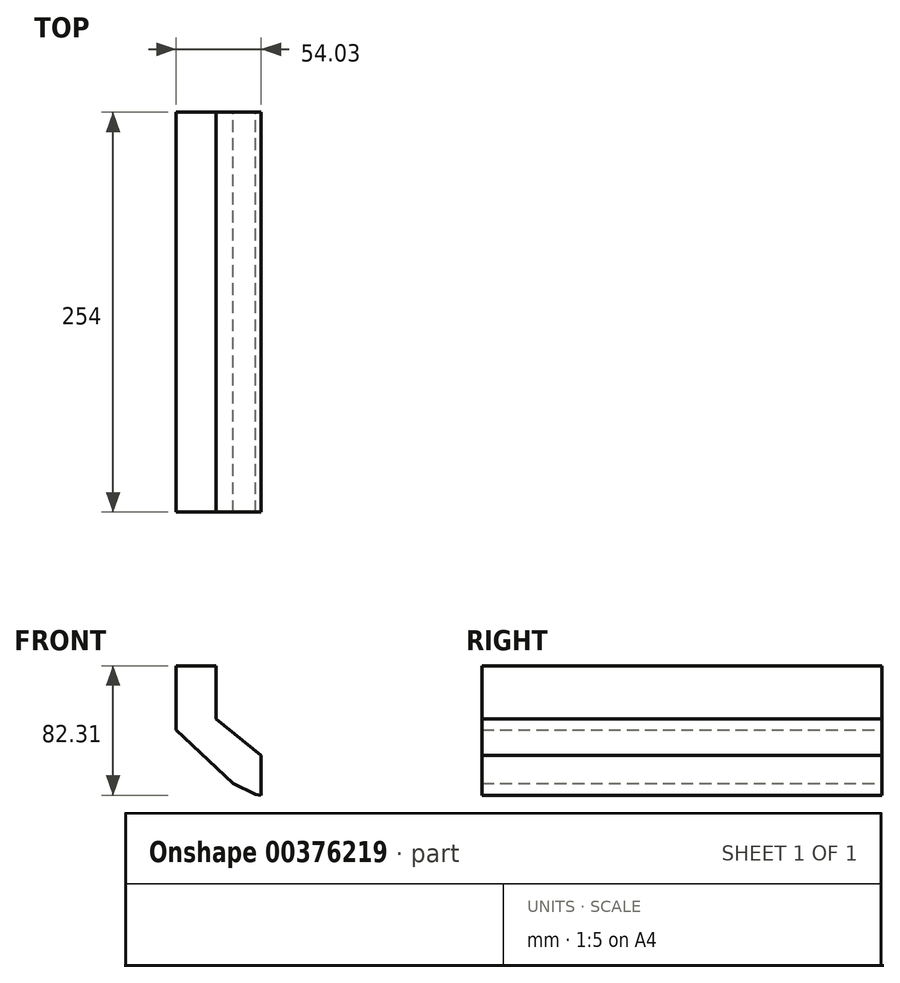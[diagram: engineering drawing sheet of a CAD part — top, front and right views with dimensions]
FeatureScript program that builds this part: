
annotation { "Feature Type Name" : "Feature", "Feature Type Description" : "" }
export const myFeature = defineFeature(function(context is Context, id is Id, definition is map)
    precondition{}
    {
        {
            var Q0;
            Q0=qCreatedBy(makeId("Front.planeOp"),FACE);
            var sketch = newSketch(context, id + "F0", { "sketchPlane" : qUnion([Q0])});
            skLineSegment(sketch, "E0", {"start": v(-75.11, 59.67) * mm, "end": v(-75.11, 18.74) * mm});
            skLineSegment(sketch, "E1", {"start": v(-75.11, 18.74) * mm, "end": v(-39.14, -14.99) * mm});
            skLineSegment(sketch, "E2", {"start": v(-39.14, -14.99) * mm, "end": v(-24.7, -22.2) * mm});
            skLineSegment(sketch, "E3", {"start": v(-75.11, 59.67) * mm, "end": v(-49.71, 59.67) * mm});
            skLineSegment(sketch, "E4", {"start": v(-21.08, 2.69) * mm, "end": v(-21.08, -22.64) * mm});
            skLineSegment(sketch, "E5", {"start": v(-21.08, -22.64) * mm, "end": v(-24.7, -22.2) * mm});
            skLineSegment(sketch, "E6", {"start": v(-49.71, 59.67) * mm, "end": v(-49.71, 25.93) * mm});
            skLineSegment(sketch, "E7", {"start": v(-49.71, 25.93) * mm, "end": v(-21.08, 2.69) * mm});
            skSolve(sketch);
        }
        {
            var Q0;
            Q0 = qSketchRegion(id + "F0", true);
            extrude(context, id + "F1", {"entities" : qUnion([Q0]), "endBound" : BoundingType.SYMMETRIC, "depth" : 254 * mm});
        }
    });
